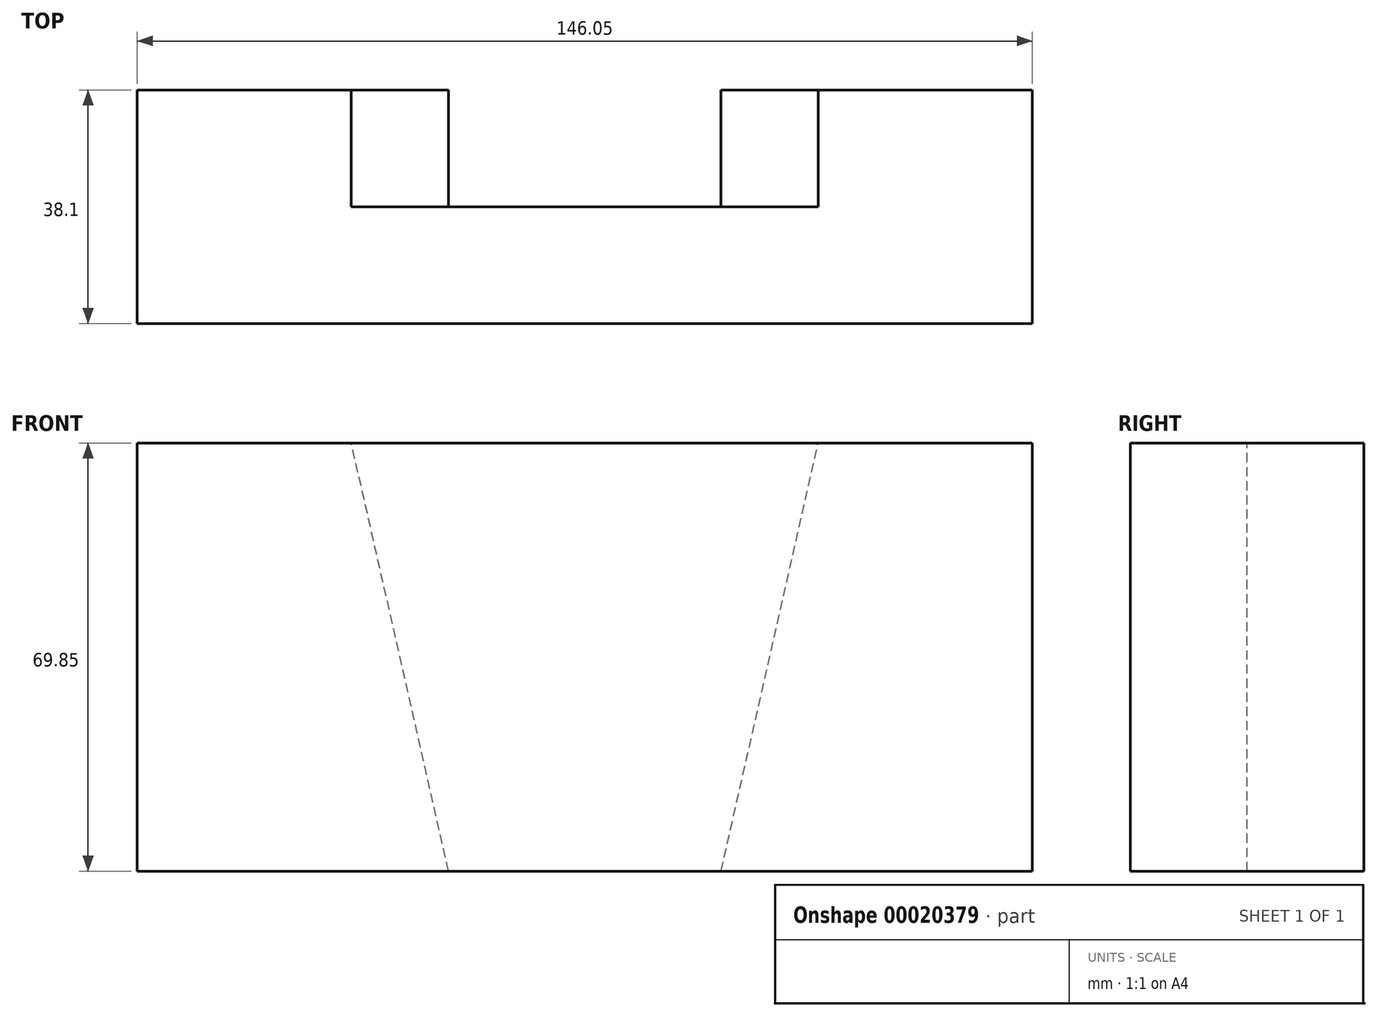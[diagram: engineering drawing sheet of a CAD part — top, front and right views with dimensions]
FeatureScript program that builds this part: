
annotation { "Feature Type Name" : "Feature", "Feature Type Description" : "" }
export const myFeature = defineFeature(function(context is Context, id is Id, definition is map)
    precondition{}
    {
        {
            var Q0;
            Q0=qCreatedBy(makeId("Front.planeOp"),FACE);
            var sketch = newSketch(context, id + "F0", { "sketchPlane" : qUnion([Q0])});
            skLineSegment(sketch, "E0.bottom", {"start": v(-111.55, 18.16) * mm, "end": v(34.5, 18.16) * mm});
            skLineSegment(sketch, "E0.top", {"start": v(-111.55, -51.69) * mm, "end": v(34.5, -51.69) * mm});
            skLineSegment(sketch, "E0.left", {"start": v(-111.55, 18.16) * mm, "end": v(-111.55, -51.69) * mm});
            skLineSegment(sketch, "E0.right", {"start": v(34.5, 18.16) * mm, "end": v(34.5, -51.69) * mm});
            skSolve(sketch);
        }
        {
            var Q0;
            Q0=makeQuery(id+"F0.imprint","IMPRINT",FACE,{"disambiguationData":[TD([[makeQuery(id+"F0.imprint","IMPRINT",EDGE,{"derivedFrom":sQuery(id+"F0.wireOp",EDGE,"E0.bottom")}),-1.0]])]});
            extrude(context, id + "F1", {"entities" : qUnion([Q0]), "depth" : 19.05 * mm});
        }
        {
            var Q0;
            Q0=makeQuery(id+"F1.opExtrude","CAP_FACE",FACE,{"disambiguationData":[OSD([sQuery(id+"F0.wireOp",EDGE,"E0.bottom"),sQuery(id+"F0.wireOp",EDGE,"E0.top"),sQuery(id+"F0.wireOp",EDGE,"E0.left"),sQuery(id+"F0.wireOp",EDGE,"E0.right")])],"isStart":true});
            var sketch = newSketch(context, id + "F2", { "sketchPlane" : qUnion([Q0])});
            skLineSegment(sketch, "E1", {"start": v(-34.5, 18.16) * mm, "end": v(-34.5, -51.69) * mm});
            skLineSegment(sketch, "E2", {"start": v(-34.5, -51.69) * mm, "end": v(16.3, -51.69) * mm});
            skLineSegment(sketch, "E3", {"start": v(16.3, -51.69) * mm, "end": v(0.42, 18.16) * mm});
            skLineSegment(sketch, "E4", {"start": v(0.42, 18.16) * mm, "end": v(-34.5, 18.16) * mm});
            skSolve(sketch);
        }
        {
            var Q0;
            Q0=makeQuery(id+"F2.imprint","IMPRINT",FACE,{"disambiguationData":[TD([[makeQuery(id+"F2.imprint","IMPRINT",EDGE,{"derivedFrom":sQuery(id+"F2.wireOp",EDGE,"E1")}),1.0]])]});
            extrude(context, id + "F3", {"entities" : qUnion([Q0]), "operationType" : NewBodyOperationType.ADD, "depth" : 19.05 * mm});
        }
        {
            var Q0;
            Q0=makeQuery(id+"F1.opExtrude","CAP_FACE",FACE,{"disambiguationData":[OSD([sQuery(id+"F0.wireOp",EDGE,"E0.bottom"),sQuery(id+"F0.wireOp",EDGE,"E0.top"),sQuery(id+"F0.wireOp",EDGE,"E0.left"),sQuery(id+"F0.wireOp",EDGE,"E0.right")])],"isStart":true});
            var sketch = newSketch(context, id + "F4", { "sketchPlane" : qUnion([Q0])});
            skLineSegment(sketch, "E5", {"start": v(111.55, 18.16) * mm, "end": v(111.55, -51.69) * mm});
            skLineSegment(sketch, "E6", {"start": v(111.55, -51.69) * mm, "end": v(60.75, -51.69) * mm});
            skLineSegment(sketch, "E7", {"start": v(60.75, -51.69) * mm, "end": v(76.62, 18.16) * mm});
            skLineSegment(sketch, "E8", {"start": v(76.62, 18.16) * mm, "end": v(111.55, 18.16) * mm});
            skSolve(sketch);
        }
        {
            var Q0;
            Q0=makeQuery(id+"F4.imprint","IMPRINT",FACE,{"disambiguationData":[TD([[makeQuery(id+"F4.imprint","IMPRINT",EDGE,{"derivedFrom":sQuery(id+"F4.wireOp",EDGE,"E5")}),-1.0]])]});
            extrude(context, id + "F5", {"entities" : qUnion([Q0]), "operationType" : NewBodyOperationType.ADD, "depth" : 19.05 * mm});
        }
    });
